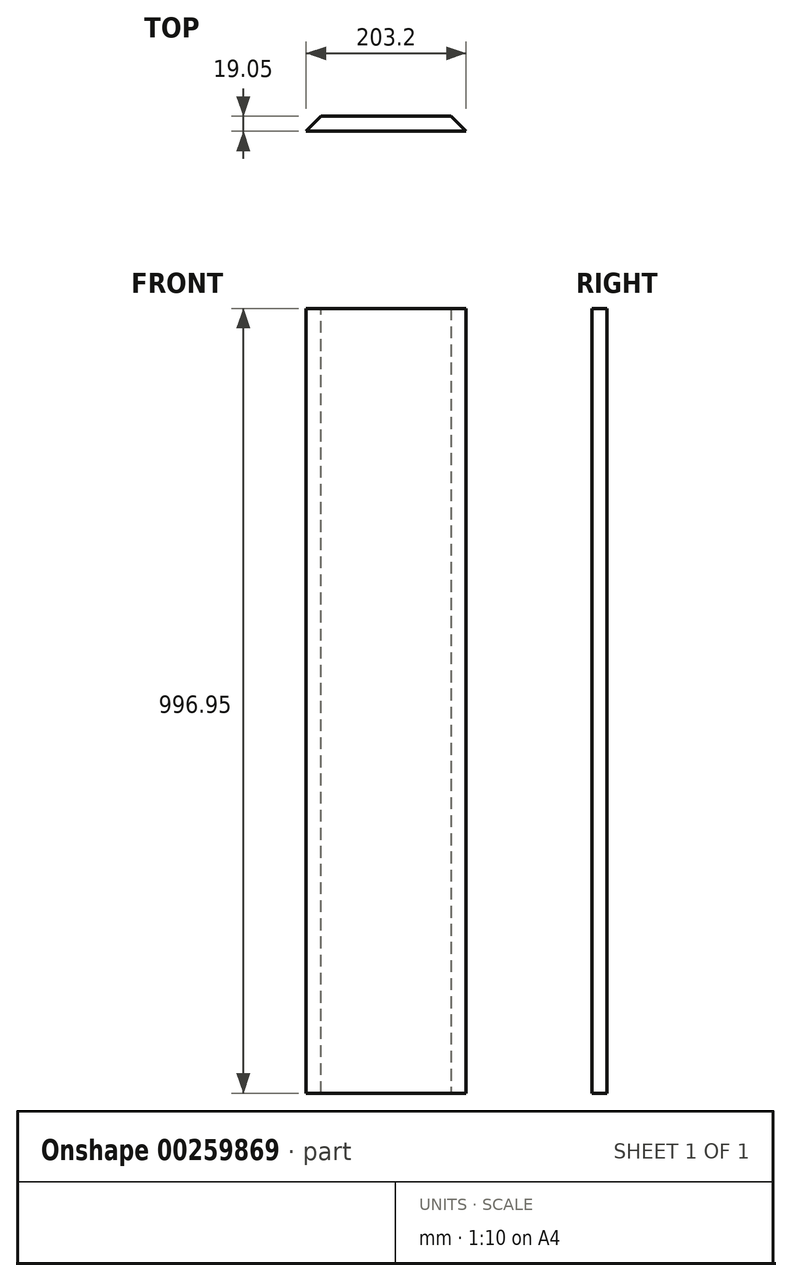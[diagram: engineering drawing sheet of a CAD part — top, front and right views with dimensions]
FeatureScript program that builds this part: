
annotation { "Feature Type Name" : "Feature", "Feature Type Description" : "" }
export const myFeature = defineFeature(function(context is Context, id is Id, definition is map)
    precondition{}
    {
        {
            var Q0;
            Q0=qCreatedBy(makeId("Front.planeOp"),FACE);
            var sketch = newSketch(context, id + "F0", { "sketchPlane" : qUnion([Q0])});
            skLineSegment(sketch, "E0.bottom", {"start": v(-101.6, 476.15) * mm, "end": v(101.6, 476.15) * mm});
            skLineSegment(sketch, "E0.top", {"start": v(-101.6, -520.8) * mm, "end": v(101.6, -520.8) * mm});
            skLineSegment(sketch, "E0.left", {"start": v(-101.6, 476.15) * mm, "end": v(-101.6, -520.8) * mm});
            skLineSegment(sketch, "E0.right", {"start": v(101.6, 476.15) * mm, "end": v(101.6, -520.8) * mm});
            skSolve(sketch);
        }
        {
            var Q0;
            Q0=makeQuery(id+"F0.imprint","IMPRINT",FACE,{"disambiguationData":[TD([[makeQuery(id+"F0.imprint","IMPRINT",EDGE,{"derivedFrom":sQuery(id+"F0.wireOp",EDGE,"E0.bottom")}),-1.0]])]});
            extrude(context, id + "F1", {"entities" : qUnion([Q0]), "depth" : 19.05 * mm});
        }
        {
            var Q0;
            Q0=makeQuery(id+"F1.opExtrude","CAP_EDGE",EDGE,{"disambiguationData":[OSD([sQuery(id+"F0.wireOp",EDGE,"E0.right")])],"isStart":true});
            var Q1;
            Q1=makeQuery(id+"F1.opExtrude","CAP_EDGE",EDGE,{"disambiguationData":[OSD([sQuery(id+"F0.wireOp",EDGE,"E0.left")])],"isStart":true});
            chamfer(context, id + "F2", {"entities" : qUnion([Q0, Q1]), "chamferType" : ChamferType.OFFSET_ANGLE, "width" : 19.05 * mm, "oppositeDirection" : false, "angle" : 45 * degree, "tangentPropagation" : true});
        }
    });
